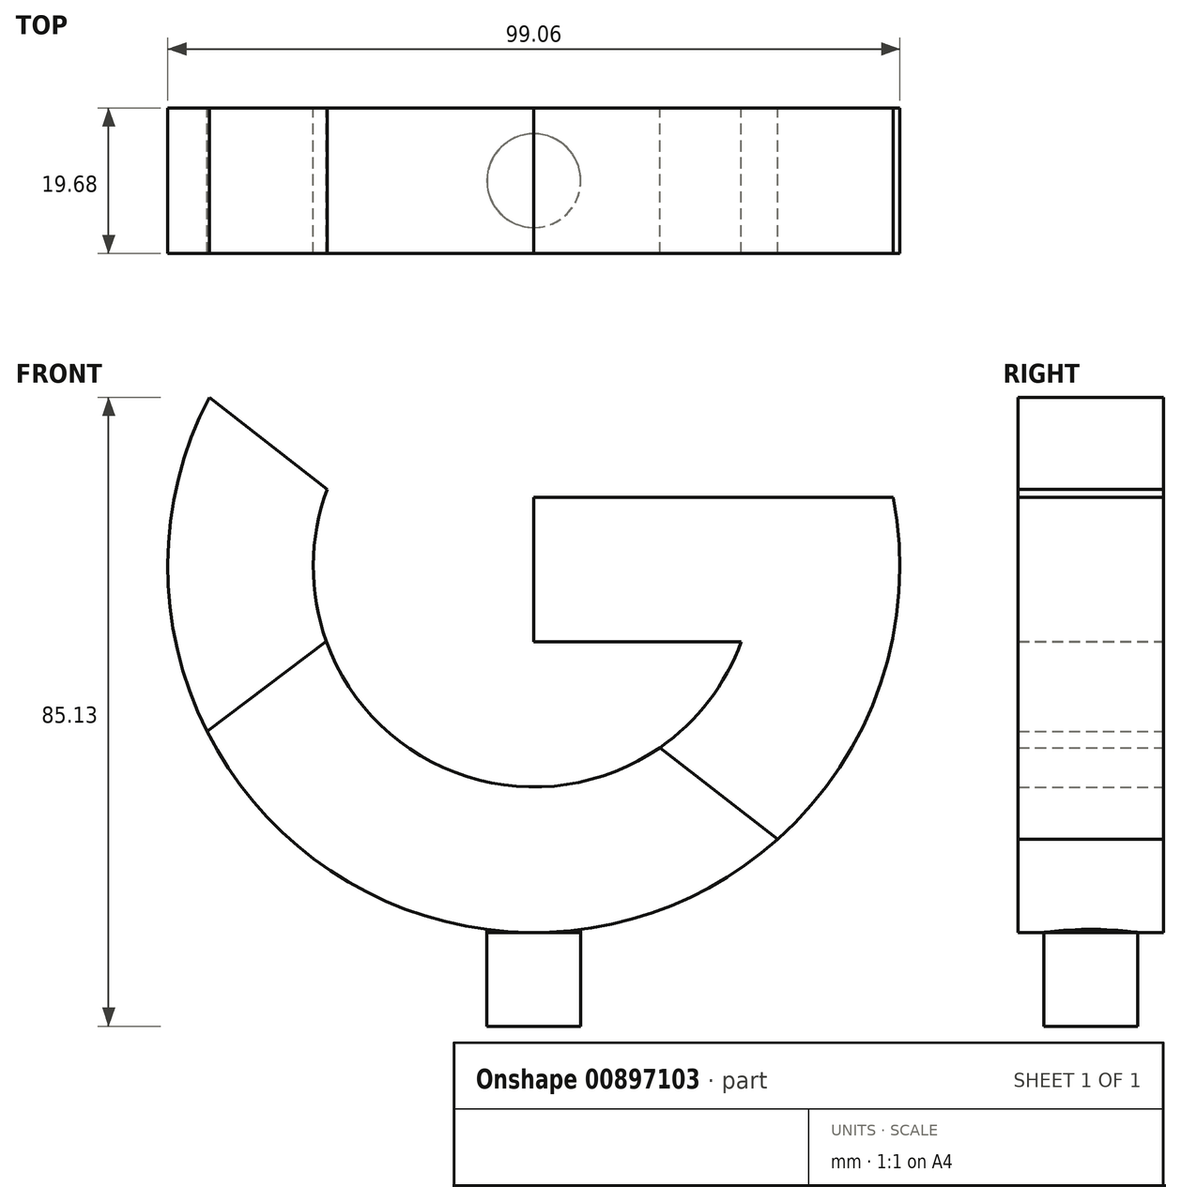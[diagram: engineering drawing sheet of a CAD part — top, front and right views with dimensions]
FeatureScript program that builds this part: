
annotation { "Feature Type Name" : "Feature", "Feature Type Description" : "" }
export const myFeature = defineFeature(function(context is Context, id is Id, definition is map)
    precondition{}
    {
        {
            var Q0;
            Q0=qCreatedBy(makeId("Front.planeOp"),FACE);
            var sketch = newSketch(context, id + "F0", { "sketchPlane" : qUnion([Q0])});
            skCircle(sketch, "E0", {"center": v(0, 0) * mm, "radius": 49.53 * mm});
            skArc(sketch, "E1", {"start": v(28.33, 9.4) * mm, "mid": v(-29.84, 0.4) * mm, "end": v(28.06, -10.16) * mm});
            skLineSegment(sketch, "E2", {"start": v(-43.92, 22.9) * mm, "end": v(33, -36.93) * mm});
            skLineSegment(sketch, "E3", {"start": v(8.46, 9.4) * mm, "end": v(33.14, 36.8) * mm});
            skLineSegment(sketch, "E4", {"start": v(-44.22, -22.32) * mm, "end": v(-28.08, -10.1) * mm});
            skLineSegment(sketch, "E5", {"start": v(48.63, 9.4) * mm, "end": v(0, 9.4) * mm});
            skLineSegment(sketch, "E6", {"start": v(0, 9.4) * mm, "end": v(0, -10.16) * mm});
            skLineSegment(sketch, "E7", {"start": v(0, -10.16) * mm, "end": v(28.06, -10.16) * mm});
            skSolve(sketch);
        }
        {
            var Q0;
            {var subQ0=sQuery(id+"F0.wireOp",EDGE,"E2");var subQ1=sQuery(id+"F0.wireOp",EDGE,"E0");var subQ2=makeQuery(id+"F0.imprint","INTERSECT",VERTEX,{"disambiguationData":[OD(0.0)],"derivedFrom":[subQ1,subQ0]});Q0=makeQuery(id+"F0.imprint","IMPRINT",FACE,{"disambiguationData":[TD([[makeQuery(id+"F0.imprint","IMPRINT",EDGE,{"disambiguationData":[TD([[subQ2,1.0]])],"derivedFrom":subQ1}),1.0]])]});}
            var Q1;
            {var subQ3=sQuery(id+"F0.wireOp",EDGE,"E4");Q1=makeQuery(id+"F0.imprint","IMPRINT",FACE,{"disambiguationData":[TD([[makeQuery(id+"F0.imprint","IMPRINT",EDGE,{"derivedFrom":subQ3}),-1.0]])]});}
            extrude(context, id + "F1", {"entities" : qUnion([Q0, Q1]), "depth" : 19.68 * mm, "offsetDistance" : 25.4 * mm, "symmetric" : true});
        }
        {
            var Q0;
            {var subQ3=sQuery(id+"F0.wireOp",EDGE,"E4");Q0=makeQuery(id+"F0.imprint","IMPRINT",FACE,{"disambiguationData":[TD([[makeQuery(id+"F0.imprint","IMPRINT",EDGE,{"derivedFrom":subQ3}),1.0]])]});}
            var Q1;
            {var subQ10=sQuery(id+"F0.wireOp",EDGE,"E6");Q1=makeQuery(id+"F0.imprint","IMPRINT",FACE,{"disambiguationData":[TD([[makeQuery(id+"F0.imprint","IMPRINT",EDGE,{"derivedFrom":subQ10}),1.0]])]});}
            extrude(context, id + "F2", {"entities" : qUnion([Q0, Q1]), "depth" : 19.68 * mm, "offsetDistance" : 25.4 * mm, "symmetric" : true});
        }
        {
            var Q0;
            Q0=qCreatedBy(makeId("Top.planeOp"),FACE);
            var sketch = newSketch(context, id + "F3", { "sketchPlane" : qUnion([Q0])});
            skCircle(sketch, "E8", {"center": v(0, 0) * mm, "radius": 6.35 * mm});
            skSolve(sketch);
        }
        {
            var Q0;
            Q0=makeQuery(id+"F3.imprint","IMPRINT",FACE,{"disambiguationData":[TD([[makeQuery(id+"F3.imprint","IMPRINT",EDGE,{"derivedFrom":sQuery(id+"F3.wireOp",EDGE,"E8")}),1.0]])]});
            extrude(context, id + "F4", {"entities" : qUnion([Q0]), "operationType" : NewBodyOperationType.ADD, "oppositeDirection" : true, "depth" : 49.53 * mm, "offsetDistance" : 25.4 * mm, "hasSecondDirection" : true, "secondDirectionOppositeDirection" : true, "secondDirectionDepth" : 45.72 * mm});
        }
        {
            var Q0;
            Q0=makeQuery(id+"F4.opExtrude","CAP_FACE",FACE,{"disambiguationData":[OSD([sQuery(id+"F3.wireOp",EDGE,"E8")])],"isStart":false});
            extrude(context, id + "F5", {"entities" : qUnion([Q0]), "depth" : 12.7 * mm, "offsetDistance" : 25.4 * mm});
        }
    });
